# Revit family: 210_Menu-M Slimline
name_source: partatom
category: Mechanical Equipment
revit_build: Autodesk Revit 2018 (Build: 20170223_1515(x64)
units: mm (PartAtom-declared; Revit-internal decimal feet)

## family parameters
Always vertical = Yes
Cut with Voids When Loaded = No
Part Type = Breaks Into
Room Calculation Point = No
Round Connector Dimension = Use Diameter
Shared = No
Work Plane-Based = No

## types (1)
- 125-13645
    CAT0 = Yes
    D = 125 mm
    Description = Ventilator Menu-M slimline
    L1 = 500 mm  [stored 1.64042 ft]
    L1T2 = 250 mm  [stored 0.82021 ft]
    L2 = 250 mm  [stored 0.82021 ft]
    L3T2 = 300 mm  [stored 0.984252 ft]
    MC Product Code = 125-13645
    Manufacturer = Flexit
    QmdConnectorList = 201;D
    W = 280 mm  [stored 0.918635 ft]
    W2 = 65 mm  [stored 0.213255 ft]
    X1 = 275 mm  [stored 0.902231 ft]
    Y1 = 270 mm  [stored 0.885827 ft]
    Y1T2 = 135 mm  [stored 0.442913 ft]
    Y2 = 152 mm  [stored 0.498688 ft]
    Z1 = 135 mm  [stored 0.442913 ft]
    Z1__ve = -135 mm  [stored -0.442913 ft]
    Z2 = 40 mm  [stored 0.131234 ft]
    Z2__ve = -40 mm  [stored -0.131234 ft]
    Z3 = 20 mm  [stored 0.0656168 ft]
    magiPartTypeId = 210
    magiProductFamilyId = Menu-M Slimline
    magiProductId = Menu-M Slimline 125

note: [stored X ft] marks values corroborated as IEEE doubles in the binary element streams (Revit-internal decimal feet)

## geometry (parser evidence)
native form markers: Sweep x2
no freeform markers — native parametric forms only
